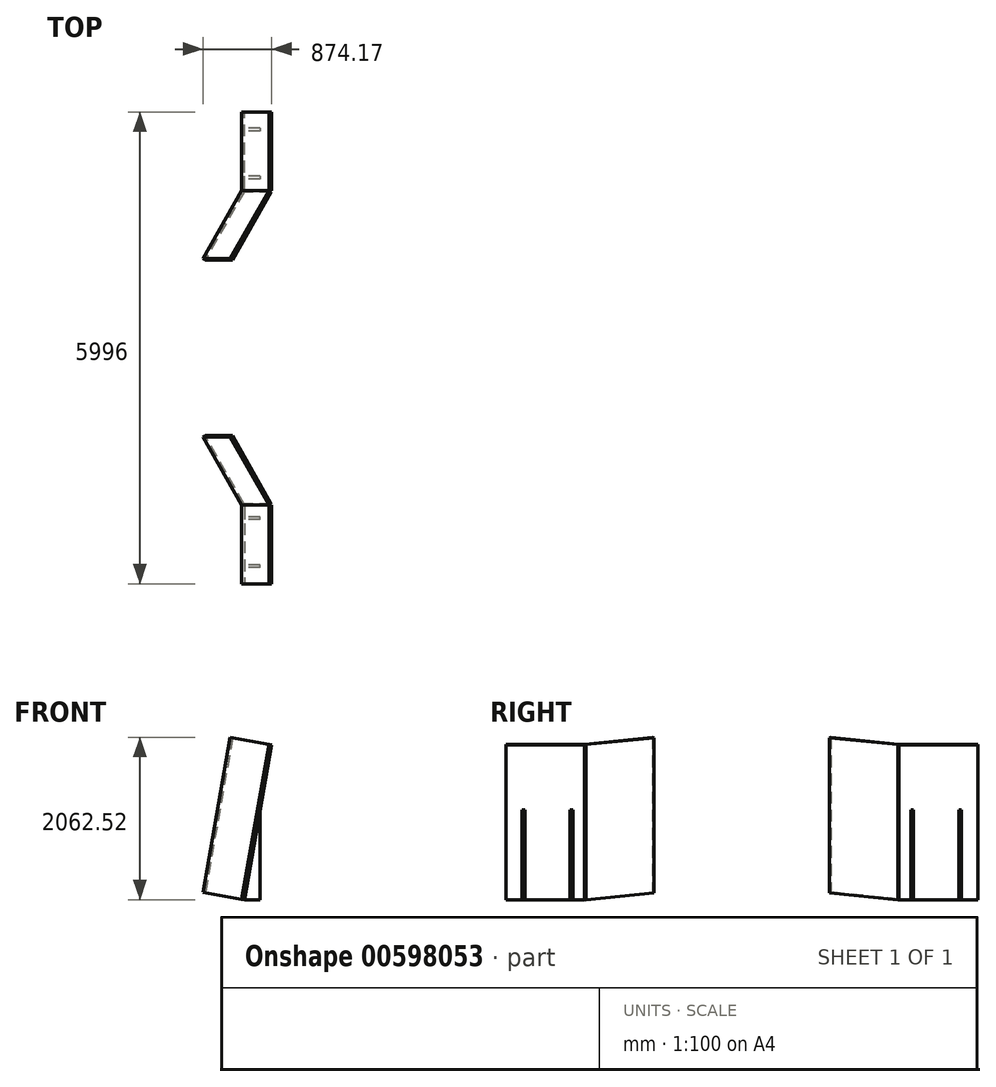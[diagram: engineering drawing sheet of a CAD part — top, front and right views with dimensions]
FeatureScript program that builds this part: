
annotation { "Feature Type Name" : "Feature", "Feature Type Description" : "" }
export const myFeature = defineFeature(function(context is Context, id is Id, definition is map)
    precondition{}
    {
        {
            var Q0;
            Q0=qCreatedBy(makeId("Top.planeOp"),FACE);
            var sketch = newSketch(context, id + "F0", { "sketchPlane" : qUnion([Q0])});
            skLineSegment(sketch, "E0.bottom", {"start": v(0, 0) * mm, "end": v(35, 0) * mm});
            skLineSegment(sketch, "E0.top", {"start": v(0, -1000) * mm, "end": v(35, -1000) * mm});
            skLineSegment(sketch, "E0.left", {"start": v(0, 0) * mm, "end": v(0, -1000) * mm});
            skLineSegment(sketch, "E0.right", {"start": v(35, 0) * mm, "end": v(35, -1000) * mm});
            skLineSegment(sketch, "E1.bottom", {"start": v(-469.69, 883.53) * mm, "end": v(-500, 866.03) * mm});
            skLineSegment(sketch, "E1.top", {"start": v(30.31, 17.5) * mm, "end": v(0, 0) * mm});
            skLineSegment(sketch, "E1.left", {"start": v(0, 0) * mm, "end": v(-500, 866.03) * mm});
            skLineSegment(sketch, "E1.right", {"start": v(30.31, 17.5) * mm, "end": v(-469.69, 883.53) * mm});
            skSolve(sketch);
        }
        {
            var Q0;
            Q0 = qSketchRegion(id + "F0", true);
            extrude(context, id + "F1", {"entities" : qUnion([Q0]), "depth" : 2000 * mm, "offsetDistance" : 25 * mm});
        }
        {
            var Q0;
            Q0=makeQuery(id+"F1.opExtrude","SWEPT_BODY",BODY,{"disambiguationData":[OSD([sQuery(id+"F0.wireOp",EDGE,"E0.bottom"),sQuery(id+"F0.wireOp",EDGE,"E0.top"),sQuery(id+"F0.wireOp",EDGE,"E0.left"),sQuery(id+"F0.wireOp",EDGE,"E0.right")])]});
            var Q1;
            Q1=makeQuery(id+"F1.opExtrude","SWEPT_BODY",BODY,{"disambiguationData":[OSD([sQuery(id+"F0.wireOp",EDGE,"E1.bottom"),sQuery(id+"F0.wireOp",EDGE,"E1.top"),sQuery(id+"F0.wireOp",EDGE,"E1.left"),sQuery(id+"F0.wireOp",EDGE,"E1.right")])]});
            var Q2;
            Q2=makeQuery(id+"F1.opExtrude","CAP_EDGE",EDGE,{"disambiguationData":[OSD([sQuery(id+"F0.wireOp",EDGE,"E0.right")])],"isStart":true});
            transform(context, id + "F2", {"entities" : qUnion([Q0, Q1]), "transformType" : TransformType.ROTATION, "transformAxis" : qUnion([Q2]), "angle" : 10 * degree, "oppositeDirection" : true, "makeCopy" : false});
        }
        {
            var Q0;
            Q0=qCreatedBy(makeId("Top.planeOp"),FACE);
            var sketch = newSketch(context, id + "F3", { "sketchPlane" : qUnion([Q0])});
            skLineSegment(sketch, "E2.bottom", {"start": v(35, -147.91) * mm, "end": v(236.35, -147.91) * mm});
            skLineSegment(sketch, "E2.top", {"start": v(35, -182.91) * mm, "end": v(236.35, -182.91) * mm});
            skLineSegment(sketch, "E2.left", {"start": v(35, -147.91) * mm, "end": v(35, -182.91) * mm});
            skLineSegment(sketch, "E2.right", {"start": v(236.35, -147.91) * mm, "end": v(236.35, -182.91) * mm});
            skSolve(sketch);
        }
        {
            var Q0;
            Q0 = qSketchRegion(id + "F3", true);
            extrude(context, id + "F4", {"entities" : qUnion([Q0]), "endBound" : BoundingType.UP_TO_NEXT, "depth" : 25 * mm, "offsetDistance" : 25 * mm});
        }
        {
            var Q0;
            Q0=makeQuery(id+"F4.opExtrude","SWEPT_BODY",BODY,{"disambiguationData":[OSD([sQuery(id+"F3.wireOp",EDGE,"E2.bottom"),sQuery(id+"F3.wireOp",EDGE,"E2.top"),sQuery(id+"F3.wireOp",EDGE,"E2.left"),sQuery(id+"F3.wireOp",EDGE,"E2.right")])]});
            transform(context, id + "F5", {"entities" : qUnion([Q0]), "transformType" : TransformType.TRANSLATION_3D, "dx" : 0 * mm, "dy" : -610 * mm, "dz" : 0 * mm, "makeCopy" : true});
        }
        {
            var Q0;
            Q0=qCreatedBy(makeId("Front.planeOp"),FACE);
            cPlane(context, id + "F6", {"entities" : qUnion([Q0]), "cplaneType" : CPlaneType.OFFSET, "offset" : 1998 * mm, "oppositeDirection" : true, "width" : 150 * mm, "height" : 150 * mm});
        }
        {
            var Q0;
            Q0=makeQuery(id+"F1.opExtrude","SWEPT_BODY",BODY,{"disambiguationData":[OSD([sQuery(id+"F0.wireOp",EDGE,"E1.bottom"),sQuery(id+"F0.wireOp",EDGE,"E1.top"),sQuery(id+"F0.wireOp",EDGE,"E1.left"),sQuery(id+"F0.wireOp",EDGE,"E1.right")])]});
            var Q1;
            Q1=makeQuery(id+"F1.opExtrude","SWEPT_BODY",BODY,{"disambiguationData":[OSD([sQuery(id+"F0.wireOp",EDGE,"E0.bottom"),sQuery(id+"F0.wireOp",EDGE,"E0.top"),sQuery(id+"F0.wireOp",EDGE,"E0.left"),sQuery(id+"F0.wireOp",EDGE,"E0.right")])]});
            var Q2;
            Q2=makeQuery(id+"F5.opPattern","COPY",BODY,{"derivedFrom":makeQuery(id+"F4.opExtrude","SWEPT_BODY",BODY,{"disambiguationData":[OSD([sQuery(id+"F3.wireOp",EDGE,"E2.bottom"),sQuery(id+"F3.wireOp",EDGE,"E2.top"),sQuery(id+"F3.wireOp",EDGE,"E2.left"),sQuery(id+"F3.wireOp",EDGE,"E2.right")])]}),"instanceName":"1"});
            var Q3;
            Q3=makeQuery(id+"F4.opExtrude","SWEPT_BODY",BODY,{"disambiguationData":[OSD([sQuery(id+"F3.wireOp",EDGE,"E2.bottom"),sQuery(id+"F3.wireOp",EDGE,"E2.top"),sQuery(id+"F3.wireOp",EDGE,"E2.left"),sQuery(id+"F3.wireOp",EDGE,"E2.right")])]});
            var Q4;
            Q4=qCreatedBy(id+"F6.planeOp",FACE);
            mirror(context, id + "F7", {"entities" : qUnion([Q0, Q1, Q2, Q3]), "mirrorPlane" : qUnion([Q4])});
        }
    });
